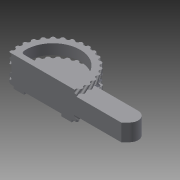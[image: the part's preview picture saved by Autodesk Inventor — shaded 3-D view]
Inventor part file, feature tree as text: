
AUTODESK INVENTOR PART (.ipt)
format: ipt  version: 2013 (Build 170138000, 138)  size: 5,554,176 bytes
history: native  units: mm
features: extrude x8, sketch x8, other x3
ambient origin geometry x8: Origin, YZ Plane, XZ Plane, XY Plane, X Axis, Y Axis, Z Axis, Center Point
bodies: Solid1 (feature_tree)
feature tree (19):
  other  "_GEARS.iam"
  other  "gear.ipt:1"
  other  "gear.ipt:2"
  extrude  "Extrusion1"  Depth=7.5mm TaperAngle=0.0deg
  extrude  "Extrusion2"  Depth=15.0mm
  extrude  "Extrusion3"  Depth=10.0mm TaperAngle=0.0deg
  extrude  "Extrusion4"  Depth=7.5mm
  extrude  "Extrusion5"  Depth=35.0mm
  extrude  "Extrusion6"  TaperAngle=135.0deg  [1 undecoded]
  extrude  "Extrusion7"  Depth=100.0mm
  extrude  "Extrusion8"  Depth=7.5mm
  sketch  "Sketch1"  dims[d0=10.0mm d1=7.5mm d3=0.0mm]
  sketch  "Sketch2"  dims[d2=60.0mm d4=15.0mm]
  sketch  "Sketch3"  dims[d5=125.0mm d6=10.0mm d7=0.0mm]
  sketch  "Sketch4"  dims[d8=48.333333mm d10=7.5mm]
  sketch  "Sketch5"  dims[d11=15.0mm d12=35.0mm]
  sketch  "Sketch6"  dims[d13=27.5mm d14=135.0deg]
  sketch  "Sketch7"  dims[d15=112.5mm d16=100.0mm]
  sketch  "Sketch8"  dims[d17=25.0mm d18=0.0mm d19=7.5mm d21=25.0mm d22=0.0mm d23=7.5mm d24=40.0mm d25=5.0mm d26=25.0mm d27=0.0mm d28=8.2mm d30=35.0mm d31=25.0mm d32=0.0mm d33=13.2mm d34=6.0mm d35=0.0mm d36=7.5mm d38=3.5mm d39=0.0mm d40=3.75mm d42=3.5mm d43=0.0mm]
note: 1 required parameter value undecoded (feature->parameter linkage not recoverable at this tier; creation-order binding heuristic only, values carry confidence <= 0.55)
